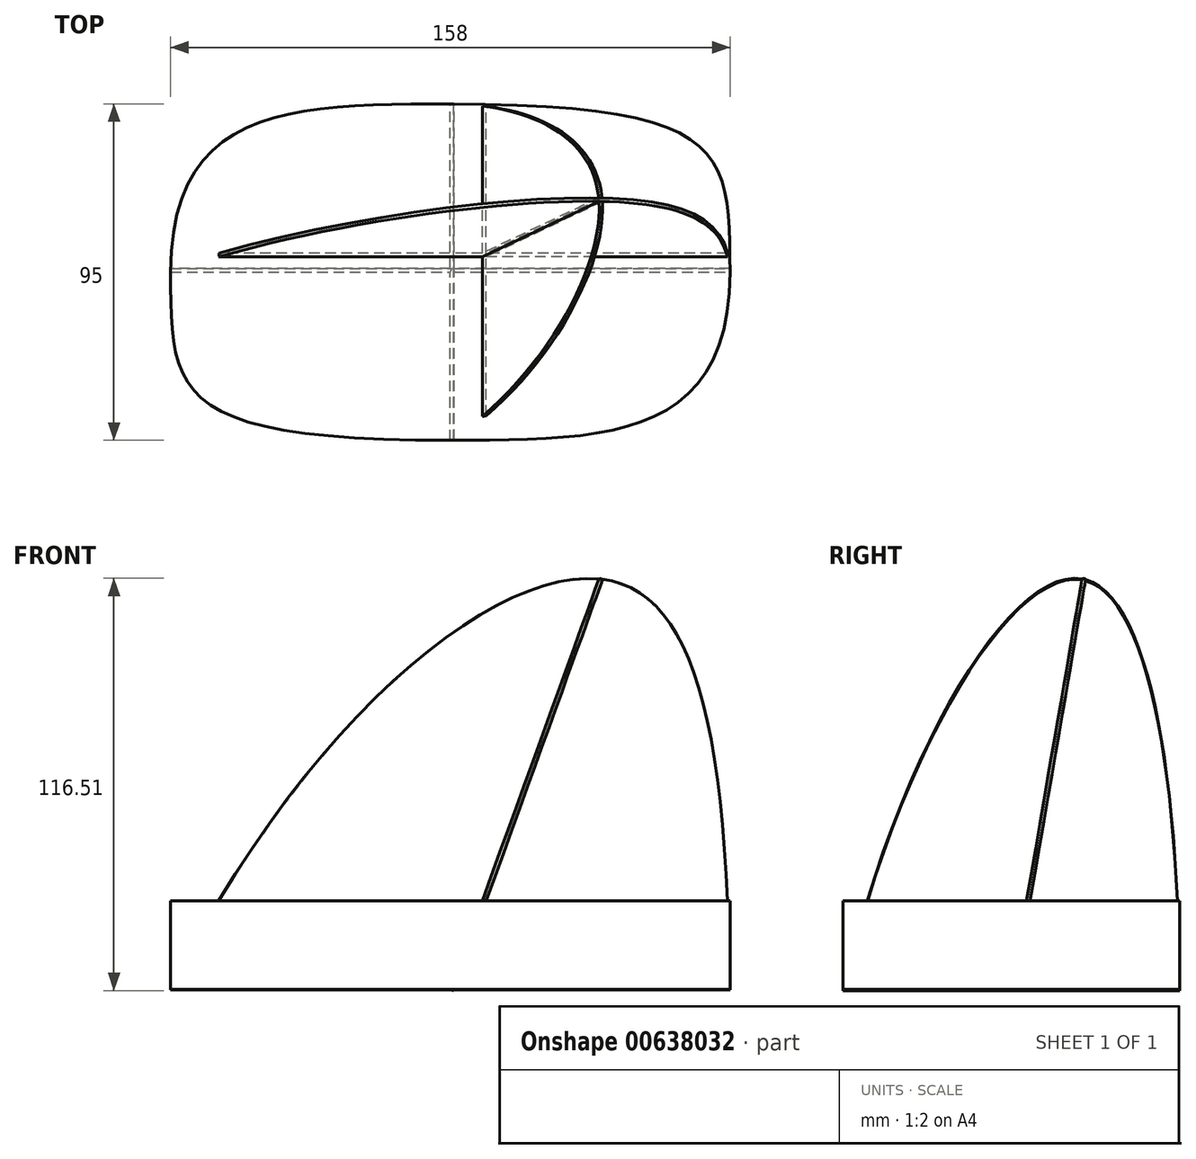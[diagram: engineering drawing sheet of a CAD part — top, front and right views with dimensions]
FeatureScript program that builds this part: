
annotation { "Feature Type Name" : "Feature", "Feature Type Description" : "" }
export const myFeature = defineFeature(function(context is Context, id is Id, definition is map)
    precondition{}
    {
        {
            var Q0;
            Q0=qCreatedBy(makeId("Top.planeOp"),FACE);
            var sketch = newSketch(context, id + "F0", { "sketchPlane" : qUnion([Q0])});
            skLineSegment(sketch, "E0.bottom", {"start": v(79, -47.5) * mm, "end": v(-79, -47.5) * mm});
            skLineSegment(sketch, "E0.top", {"start": v(79, 47.5) * mm, "end": v(-79, 47.5) * mm});
            skLineSegment(sketch, "E0.left", {"start": v(79, -47.5) * mm, "end": v(79, 47.5) * mm});
            skLineSegment(sketch, "E0.right", {"start": v(-79, -47.5) * mm, "end": v(-79, 47.5) * mm});
            skPoint(sketch, "E0.middle", {"position": v(0, 0) * mm});
            skFitSpline(sketch, "E1", {"points": [v(0, 47.5) * mm, v(-79, 0) * mm], "startDerivative": vector(-130.45, 0) * mm, "endDerivative": vector(0, -142.5) * mm});
            skFitSpline(sketch, "E2", {"points": [v(0, -47.5) * mm, v(-79, 0) * mm], "startDerivative": vector(-237, 0) * mm, "endDerivative": vector(0, 102.5) * mm});
            skFitSpline(sketch, "E3.MirrorCS", {"points": [v(0, -47.5) * mm, v(79, 0) * mm], "startDerivative": vector(130.45, 0) * mm, "endDerivative": vector(0, 142.5) * mm});
            skFitSpline(sketch, "E4.MirrorCS", {"points": [v(0, 47.5) * mm, v(79, 0) * mm], "startDerivative": vector(237, 0) * mm, "endDerivative": vector(0, -102.5) * mm});
            skSolve(sketch);
        }
        {
            var Q0;
            Q0=qCreatedBy(makeId("Front.planeOp"),FACE);
            cPlane(context, id + "F1", {"entities" : qUnion([Q0]), "cplaneType" : CPlaneType.OFFSET, "offset" : 20 * mm, "oppositeDirection" : true, "width" : 150 * mm, "height" : 150 * mm});
        }
        {
            var Q0;
            Q0=qCreatedBy(id+"F1.planeOp",FACE);
            var sketch = newSketch(context, id + "F2", { "sketchPlane" : qUnion([Q0])});
            skPoint(sketch, "E5", {"position": v(42, 116) * mm});
            skSolve(sketch);
        }
        {
            var Q0;
            Q0=sQuery(id+"F0.wireOp",EDGE,"E0.right");
            cPoint(context, id + "F3", {"entities" : qUnion([Q0]), "parameter" : 0.5});
        }
        {
            var Q0;
            Q0=sQuery(id+"F0.wireOp",EDGE,"E0.left");
            cPoint(context, id + "F4", {"entities" : qUnion([Q0]), "parameter" : 0.5});
        }
        {
            var Q0;
            Q0=sQuery(id+"F2.wireOp",VERTEX,"E5");
            var Q1;
            Q1 = qCreatedBy(id + "F3" ,VERTEX);
            var Q2;
            Q2 = qCreatedBy(id + "F4" ,VERTEX);
            cPlane(context, id + "F5", {"entities" : qUnion([Q0, Q1, Q2]), "cplaneType" : CPlaneType.THREE_POINT, "offset" : 25 * mm, "width" : 150 * mm, "height" : 150 * mm});
        }
        {
            var Q0;
            Q0=qCreatedBy(id+"F5.planeOp",FACE);
            var sketch = newSketch(context, id + "F6", { "sketchPlane" : qUnion([Q0])});
            skPoint(sketch, "E6.0", {"position": v(-42, 117.71) * mm});
            skPoint(sketch, "E7.0", {"position": v(-79, 0) * mm});
            skPoint(sketch, "E7.1", {"position": v(79, 0) * mm});
            skFitSpline(sketch, "E8", {"points": [v(-79, 0) * mm, v(-42, 117.71) * mm, v(79, 0) * mm], "startDerivative": vector(5.48, 503.93) * mm, "endDerivative": vector(204.02, -419.82) * mm});
            skLineSegment(sketch, "E9", {"start": v(79, 0) * mm, "end": v(-79, 0) * mm});
            skSolve(sketch);
        }
        {
            var Q0;
            Q0=sQuery(id+"F0.wireOp",EDGE,"E0.top");
            cPoint(context, id + "F7", {"entities" : qUnion([Q0]), "parameter" : 0.5});
        }
        {
            var Q0;
            Q0 = qCreatedBy(id + "F7" ,VERTEX);
            var Q1;
            Q1=sQuery(id+"F0.wireOp",VERTEX,"E2.start");
            var Q2;
            Q2=sQuery(id+"F2.wireOp",VERTEX,"E5");
            cPlane(context, id + "F8", {"entities" : qUnion([Q0, Q1, Q2]), "cplaneType" : CPlaneType.THREE_POINT, "offset" : 25 * mm, "width" : 150 * mm, "height" : 150 * mm});
        }
        {
            var Q0;
            Q0=qCreatedBy(id+"F8.planeOp",FACE);
            var sketch = newSketch(context, id + "F9", { "sketchPlane" : qUnion([Q0])});
            skPoint(sketch, "E10.0", {"position": v(-47.5, 0) * mm});
            skPoint(sketch, "E10.1", {"position": v(20, 123.37) * mm});
            skPoint(sketch, "E10.2", {"position": v(47.5, 0) * mm});
            skFitSpline(sketch, "E11", {"points": [v(47.5, 0) * mm, v(20, 123.37) * mm, v(-47.5, 0) * mm], "startDerivative": vector(-1.55, 395.1) * mm, "endDerivative": vector(-93.8, -425.14) * mm});
            skLineSegment(sketch, "E12", {"start": v(20, 123.37) * mm, "end": v(0, 0) * mm});
            skLineSegment(sketch, "E13", {"start": v(-47.5, 0) * mm, "end": v(47.5, 0) * mm});
            skSolve(sketch);
        }
        {
            var Q0;
            Q0=makeQuery(id+"F0.imprint","IMPRINT",FACE,{"disambiguationData":[TD([[makeQuery(id+"F0.imprint","IMPRINT",EDGE,{"derivedFrom":sQuery(id+"F0.wireOp",EDGE,"E1")}),1.0]])]});
            cPlane(context, id + "F10", {"entities" : qUnion([Q0]), "cplaneType" : CPlaneType.OFFSET, "offset" : 100 * mm, "width" : 150 * mm, "height" : 150 * mm});
        }
        {
            var Q0;
            Q0=qCreatedBy(id+"F10.planeOp",FACE);
            var sketch = newSketch(context, id + "F11", { "sketchPlane" : qUnion([Q0])});
            skFitSpline(sketch, "E14.0", {"points": [v(79, 0) * mm, v(78.16, 13.15) * mm, v(56.9, 27.07) * mm, v(-42.34, 12.82) * mm, v(-79, 0) * mm]});
            skPoint(sketch, "E15", {"position": v(-0.42, 17.24) * mm});
            skFitSpline(sketch, "E16.0", {"points": [v(79, 0) * mm, v(78.16, 13.15) * mm, v(56.9, 27.07) * mm, v(-42.34, 12.82) * mm, v(-79, 0) * mm]});
            skFitSpline(sketch, "E16.1", {"points": [v(0, 47.5) * mm, v(21.82, 47.25) * mm, v(60.81, 30.02) * mm, v(24.77, -31.45) * mm, v(0, -47.5) * mm]});
            skFitSpline(sketch, "E16.2", {"points": [v(0, 47.5) * mm, v(21.82, 47.25) * mm, v(60.81, 30.02) * mm, v(24.77, -31.45) * mm, v(0, -47.5) * mm]});
            skPoint(sketch, "E17", {"position": v(36.2, -4.99) * mm});
            skPoint(sketch, "E18", {"position": v(36.2, 34.59) * mm});
            skPoint(sketch, "E19", {"position": v(64.17, 17.24) * mm});
            skFitSpline(sketch, "E20", {"points": [v(36.2, 34.59) * mm, v(-0.42, 17.24) * mm, v(36.2, -4.99) * mm], "startDerivative": vector(-142.2, 0) * mm, "endDerivative": vector(162.05, 0) * mm});
            skFitSpline(sketch, "E21", {"points": [v(36.2, 34.59) * mm, v(64.17, 17.24) * mm, v(36.2, -4.99) * mm], "startDerivative": vector(113.9, 0) * mm, "endDerivative": vector(-141.31, 0) * mm});
            skSolve(sketch);
        }
        {
            var Q0;
            Q0=qCreatedBy(id+"F10.planeOp",FACE);
            var sketch = newSketch(context, id + "F12", { "sketchPlane" : qUnion([Q0])});
            skFitSpline(sketch, "E22.0", {"points": [v(36.2, 34.59) * mm, v(12.84, 34.59) * mm, v(-11.74, 19.13) * mm, v(8.82, -4.99) * mm, v(36.2, -4.99) * mm]});
            skFitSpline(sketch, "E22.1", {"points": [v(36.2, 34.59) * mm, v(54.8, 34.59) * mm, v(70.93, 18.87) * mm, v(60.24, -4.99) * mm, v(36.2, -4.99) * mm]});
            skPoint(sketch, "E23", {"position": v(-0.42, 17.24) * mm});
            skPoint(sketch, "E24", {"position": v(64.17, 17.24) * mm});
            skSolve(sketch);
        }
        {
            var Q0;
            Q0=qCreatedBy(id+"F5.planeOp",FACE);
            var sketch = newSketch(context, id + "F13", { "sketchPlane" : qUnion([Q0])});
            skFitSpline(sketch, "E25.0", {"points": [v(-79, 0) * mm, v(-78.16, 77.42) * mm, v(-56.9, 159.34) * mm, v(42.34, 75.44) * mm, v(79, 0) * mm]});
            skFitSpline(sketch, "E25.1", {"points": [v(-79, 0) * mm, v(-78.16, 77.42) * mm, v(-56.9, 159.34) * mm, v(42.34, 75.44) * mm, v(79, 0) * mm]});
            skPoint(sketch, "E25.2", {"position": v(-64.17, 101.48) * mm});
            skPoint(sketch, "E25.3", {"position": v(0.42, 101.48) * mm});
            skFitSpline(sketch, "E26", {"points": [v(-79, 0) * mm, v(-78.16, 77.42) * mm, v(-56.9, 159.34) * mm, v(42.34, 75.44) * mm, v(79, 0) * mm]});
            skFitSpline(sketch, "E27", {"points": [v(-79, 0) * mm, v(-78.16, 77.42) * mm, v(-56.9, 159.34) * mm, v(42.34, 75.44) * mm, v(79, 0) * mm]});
            skSolve(sketch);
        }
        {
            var Q0;
            Q0=qCreatedBy(id+"F8.planeOp",FACE);
            var sketch = newSketch(context, id + "F14", { "sketchPlane" : qUnion([Q0])});
            skFitSpline(sketch, "E28.0", {"points": [v(47.5, 0) * mm, v(47.25, 64.1) * mm, v(30.02, 178.63) * mm, v(-31.45, 72.75) * mm, v(-47.5, 0) * mm]});
            skFitSpline(sketch, "E28.1", {"points": [v(47.5, 0) * mm, v(47.25, 64.1) * mm, v(30.02, 178.63) * mm, v(-31.45, 72.75) * mm, v(-47.5, 0) * mm]});
            skPoint(sketch, "E29.0", {"position": v(34.59, 106.35) * mm});
            skPoint(sketch, "E29.1", {"position": v(-4.99, 106.35) * mm});
            skFitSpline(sketch, "E30", {"points": [v(47.5, 0) * mm, v(47.25, 64.1) * mm, v(30.02, 178.63) * mm, v(-31.45, 72.75) * mm, v(-47.5, 0) * mm]});
            skFitSpline(sketch, "E31", {"points": [v(47.5, 0) * mm, v(47.25, 64.1) * mm, v(30.02, 178.63) * mm, v(-31.45, 72.75) * mm, v(-47.5, 0) * mm]});
            skSolve(sketch);
        }
        {
            var Q0;
            Q0=makeQuery(id+"F0.imprint","IMPRINT",FACE,{"disambiguationData":[TD([[makeQuery(id+"F0.imprint","IMPRINT",EDGE,{"derivedFrom":sQuery(id+"F0.wireOp",EDGE,"E1")}),1.0]])]});
            extrude(context, id + "F15", {"entities" : qUnion([Q0]), "depth" : 25 * mm, "offsetDistance" : 25 * mm});
        }
        {
            var Q0;
            Q0=makeQuery(id+"F6.imprint","IMPRINT",FACE,{"disambiguationData":[TD([[makeQuery(id+"F6.imprint","IMPRINT",EDGE,{"derivedFrom":sQuery(id+"F6.wireOp",EDGE,"E8")}),-1.0]])]});
            extrude(context, id + "F16", {"entities" : qUnion([Q0]), "operationType" : NewBodyOperationType.ADD, "depth" : 1 * mm, "offsetDistance" : 25 * mm});
        }
        {
            var Q0;
            {var subQ0=sQuery(id+"F9.wireOp",EDGE,"E12");Q0=makeQuery(id+"F9.imprint","IMPRINT",FACE,{"disambiguationData":[TD([[makeQuery(id+"F9.imprint","IMPRINT",EDGE,{"derivedFrom":subQ0}),-1.0]])]});}
            var Q1;
            {var subQ0=sQuery(id+"F9.wireOp",EDGE,"E11");Q1=makeQuery(id+"F9.imprint","IMPRINT",FACE,{"disambiguationData":[TD([[makeQuery(id+"F9.imprint","IMPRINT",EDGE,{"derivedFrom":subQ0}),1.0]])]});}
            extrude(context, id + "F17", {"entities" : qUnion([Q0, Q1]), "operationType" : NewBodyOperationType.ADD, "depth" : 1 * mm, "offsetDistance" : 25 * mm});
        }
    });
